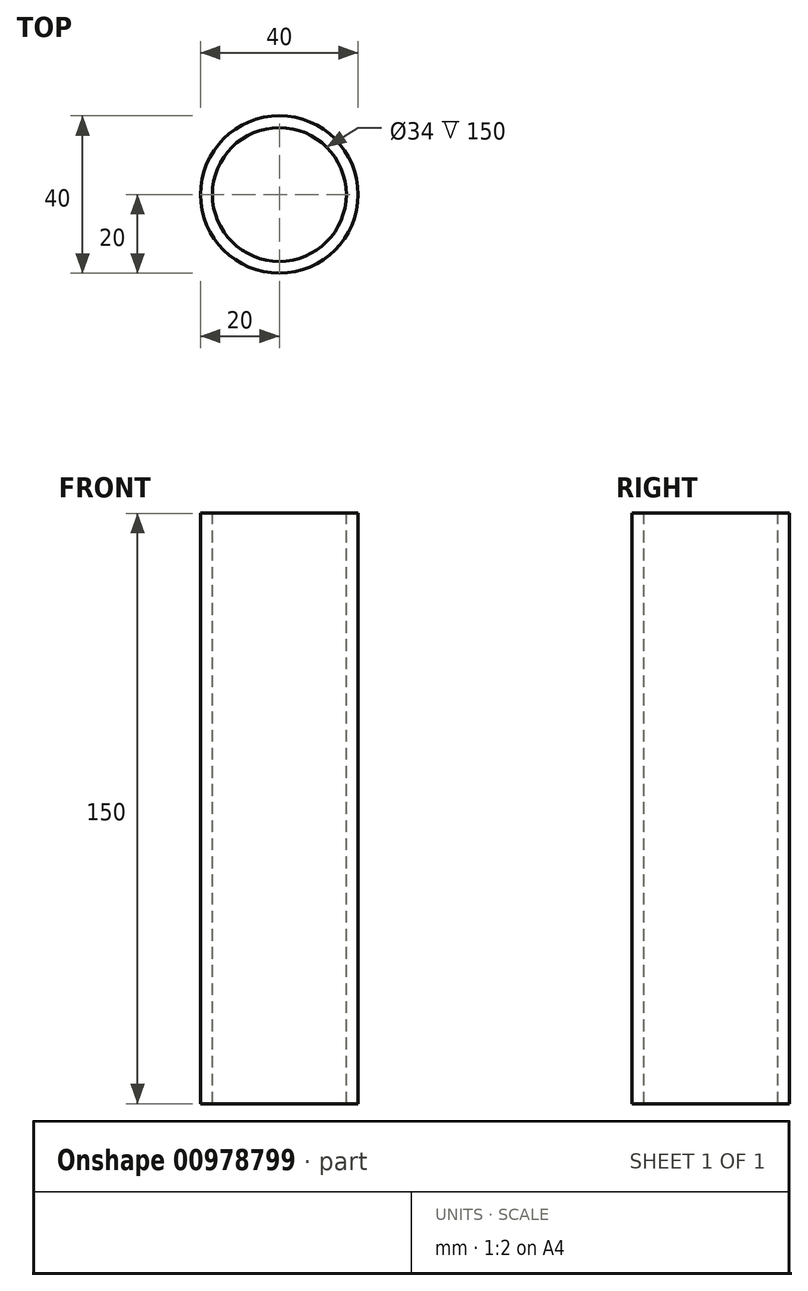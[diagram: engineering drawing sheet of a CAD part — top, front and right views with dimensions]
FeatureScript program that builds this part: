
annotation { "Feature Type Name" : "Feature", "Feature Type Description" : "" }
export const myFeature = defineFeature(function(context is Context, id is Id, definition is map)
    precondition{}
    {
        {
            var Q0;
            Q0=qCreatedBy(makeId("Right.planeOp"),FACE);
            var sketch = newSketch(context, id + "F0", { "sketchPlane" : qUnion([Q0])});
            skLineSegment(sketch, "E0", {"start": v(0, 88.69) * mm, "end": v(0, -95.8) * mm, "construction": true});
            skLineSegment(sketch, "E1.bottom", {"start": v(-20, 73.63) * mm, "end": v(-17, 73.63) * mm});
            skLineSegment(sketch, "E1.top", {"start": v(-20, -76.37) * mm, "end": v(-17, -76.37) * mm});
            skLineSegment(sketch, "E1.left", {"start": v(-20, 73.63) * mm, "end": v(-20, -76.37) * mm});
            skLineSegment(sketch, "E1.right", {"start": v(-17, 73.63) * mm, "end": v(-17, -76.37) * mm});
            skSolve(sketch);
        }
        {
            var Q0;
            Q0=makeQuery(id+"F0.imprint","IMPRINT",FACE,{"disambiguationData":[TD([[makeQuery(id+"F0.imprint","IMPRINT",EDGE,{"derivedFrom":sQuery(id+"F0.wireOp",EDGE,"E1.bottom")}),-1.0]])]});
            var Q1;
            Q1=sQuery(id+"F0.wireOp",EDGE,"E0");
            revolve(context, id + "F1", {"surfaceOperationType" : NewSurfaceOperationType.NEW, "entities" : qUnion([Q0]), "axis" : qUnion([Q1]), "revolveType" : RevolveType.FULL});
        }
    });
